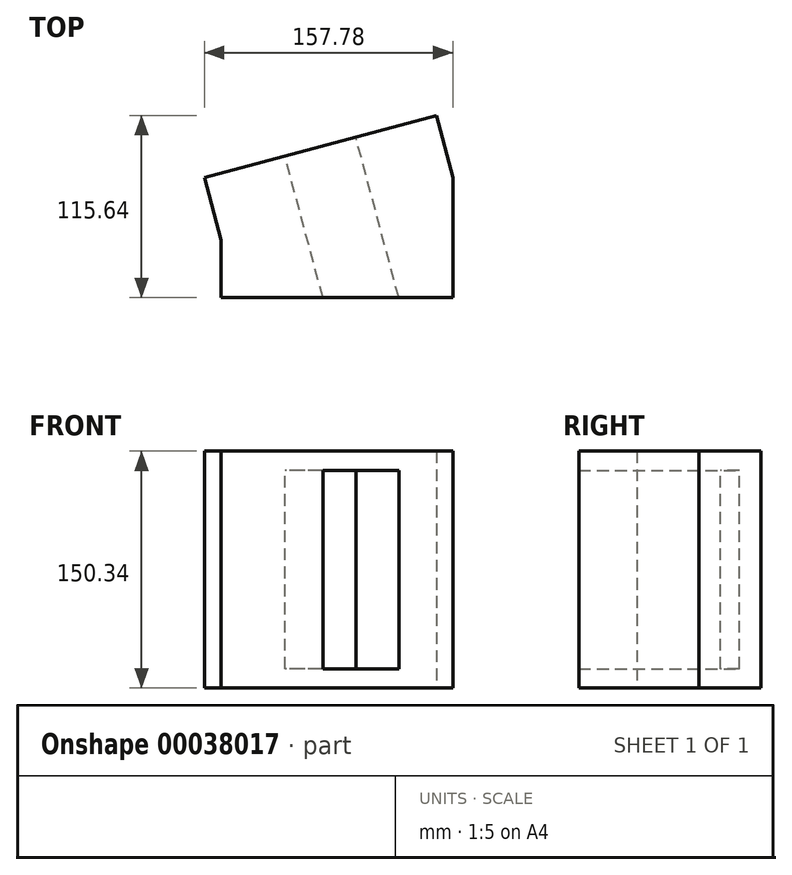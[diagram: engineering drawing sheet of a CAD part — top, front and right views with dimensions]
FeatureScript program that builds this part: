
annotation { "Feature Type Name" : "Feature", "Feature Type Description" : "" }
export const myFeature = defineFeature(function(context is Context, id is Id, definition is map)
    precondition{}
    {
        {
            var Q0;
            Q0=qCreatedBy(makeId("Top.planeOp"),FACE);
            var sketch = newSketch(context, id + "F0", { "sketchPlane" : qUnion([Q0])});
            skLineSegment(sketch, "E0", {"start": v(0, 0) * mm, "end": v(-147.2, -39.44) * mm});
            skLineSegment(sketch, "E1", {"start": v(0, 0) * mm, "end": v(10.57, -39.44) * mm});
            skLineSegment(sketch, "E2", {"start": v(10.57, -39.44) * mm, "end": v(10.57, -115.64) * mm});
            skLineSegment(sketch, "E3", {"start": v(10.57, -115.64) * mm, "end": v(-136.64, -115.64) * mm});
            skLineSegment(sketch, "E4", {"start": v(-147.2, -39.44) * mm, "end": v(10.57, -39.44) * mm, "construction": true});
            skLineSegment(sketch, "E5", {"start": v(-147.2, -39.44) * mm, "end": v(-136.64, -78.89) * mm});
            skLineSegment(sketch, "E6", {"start": v(-136.64, -78.89) * mm, "end": v(-136.64, -115.64) * mm});
            skSolve(sketch);
        }
        {
            var Q0;
            Q0 = qSketchRegion(id + "F0", true);
            extrude(context, id + "F1", {"entities" : qUnion([Q0]), "depth" : 150.34 * mm});
        }
        {
            var Q0;
            Q0=makeQuery(id+"F1.opExtrude","SWEPT_FACE",FACE,{"disambiguationData":[OSD([sQuery(id+"F0.wireOp",EDGE,"E0")])]});
            var sketch = newSketch(context, id + "F2", { "sketchPlane" : qUnion([Q0])});
            skLineSegment(sketch, "E7", {"start": v(0, 75.17) * mm, "end": v(152.4, 75.17) * mm, "construction": true});
            skLineSegment(sketch, "E8.rect.bottom", {"start": v(52.92, 12.14) * mm, "end": v(99.48, 12.14) * mm});
            skLineSegment(sketch, "E8.rect.top", {"start": v(52.92, 138.2) * mm, "end": v(99.48, 138.2) * mm});
            skLineSegment(sketch, "E8.rect.left", {"start": v(52.92, 12.14) * mm, "end": v(52.92, 138.2) * mm});
            skLineSegment(sketch, "E8.rect.right", {"start": v(99.48, 12.14) * mm, "end": v(99.48, 138.2) * mm});
            skPoint(sketch, "E8.rect.middle", {"position": v(76.2, 75.17) * mm});
            skSolve(sketch);
        }
        {
            var Q0;
            Q0 = qSketchRegion(id + "F2", true);
            var Q1;
            Q1=makeQuery(id+"F1.opExtrude","SWEPT_FACE",FACE,{"disambiguationData":[OSD([sQuery(id+"F0.wireOp",EDGE,"E3")])]});
            extrude(context, id + "F3", {"entities" : qUnion([Q0]), "operationType" : NewBodyOperationType.REMOVE, "endBound" : BoundingType.UP_TO_SURFACE, "oppositeDirection" : true, "endBoundEntityFace" : qUnion([Q1]), "depth" : 25.4 * mm});
        }
    });
